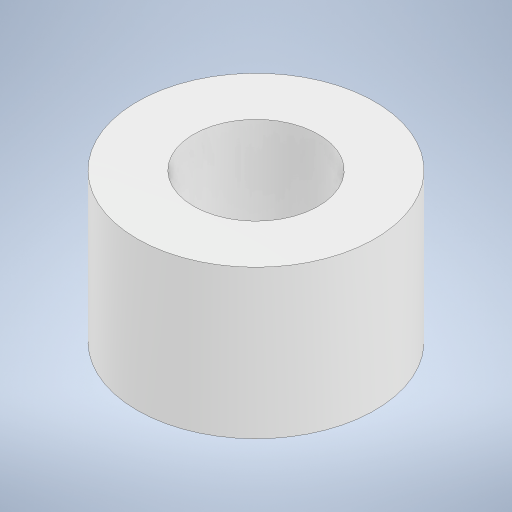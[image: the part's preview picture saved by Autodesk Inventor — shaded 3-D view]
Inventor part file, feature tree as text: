
AUTODESK INVENTOR PART (.ipt)
format: ipt  version: 2024.2 (Build 282272000, 272)  size: 218,112 bytes
history: native  units: mm
features: revolve x1, sketch x1
ambient origin geometry x8: Origin, YZ Plane, XZ Plane, XY Plane, X Axis, Y Axis, Z Axis, Center Point
bodies: Solid1 (feature_tree)
feature tree (2):
  revolve  "Revolution1"  [1 undecoded]
  sketch  "Sketch1"  dims[d0=2.5mm d1=2.1mm d2=4.0mm d3=90.0deg]
note: 1 required parameter value undecoded (feature->parameter linkage not recoverable at this tier; creation-order binding heuristic only, values carry confidence <= 0.55)
